# Revit family: Plumbing-Flushometer-Sloan-Valve-NAVAL-111_
name_source: partatom
category: Plumbing Fixtures
units: mm (PartAtom-declared; Revit-internal decimal feet)

## family parameters
Cut with Voids When Loaded = No
Host = Face
OmniClass Number = 23.45.05.14.99
OmniClass Title = Other Sanitary Washing Plumbing Fixtures
Part Type = Normal
Room Calculation Point = No
Round Connector Dimension = Use Diameter
Shared = No

## types (6) — shared parameters
Assembly Code = D2020300
CW Connection = Yes
Centerline of Supply from Top of Fixture = 11 1/2"
Centerline of Supply to Centerline of Valve = 4 3/4"
Default Elevation = 0"
Edition number = 1
Flush Rate = 1.6 gpf (6.0 Lpf)
HW Connection = No
Height = 14 3/8"
Keynote = 15410
Manufacturer = Sloan Valve
Operating Water Pressure = 15 – 80 PSI (103 – 552 kPa)
Product Material = Sloan Valve - Finish - Polished Chrome
Product data url = https://bimobject.com
URL = www.sloanvalve.com
Valve Pressure Drop = 0.00 psi
Vent Connection = No
Waste Connection = No
Water Inlet Connection Description = Water Inlet Connection
Water Inlet Connection Diameter = 1"
zero-valued in all types: CWFU, HWFU, WFU

## per-type parameters (varying)
| type | Description | Model | Part Number |
| NAVAL 111-1.6 | 1.6 gpf, Polished Chrome Finish, Fixture Connection Top Spud, Single Flush, Naval Exposed Manual Water Closet Flushometer. | NAVAL 111-1.6 | 3140011 |
| NAVAL 111-1.6-GJ-XYV | 1.6 gpf, Polished Chrome Finish, Fixture Connection Top Spud, Single Flush, Ground Joint Control Stop, Less Vacuum Breaker, Naval Exposed Manual Water Closet Flushometer. | NAVAL 111-1.6-GJ-XYV | 3140030 |
| NAVAL 111-1.6 - Shower piston assembly | 1.6 gpf, Polished Chrome Finish, Fixture Connection Top Spud, Single Flush, Naval Exposed Manual Water Closet Flushometer. | NAVAL 111-1.6 | 3148000 |
| NAVAL 111-1.6-XYV | 1.6 gpf, Polished Chrome Finish, Fixture Connection Top Spud, Single Flush, Less Vacuum Breaker, Naval Exposed Manual Water Closet Flushometer. | NAVAL 111-1.6-XYV | 3140035 |
| NAVAL 111-1.6-L/STOP-XYV | 1.6 gpf, Polished Chrome Finish, Fixture Connection Top Spud, Single Flush, Less Control Stop, Less Vacuum Breaker, Naval Exposed Manual Water Closet Flushometer. | NAVAL 111-1.6-L/STOP-XYV | 3140036 |
| NAVAL 111-1.6-U-XYV | 1.6 gpf, Polished Chrome Finish, 1.25" Flush Connection, Fixture Connection Top Spud, Single Flush, Less Vacuum Breaker, Naval Exposed Manual Water Closet Flushometer. | NAVAL 111-1.6-U-XYV | 3140037 |

## geometry (parser evidence)
native form markers: Sweep x4
no freeform markers — native parametric forms only
